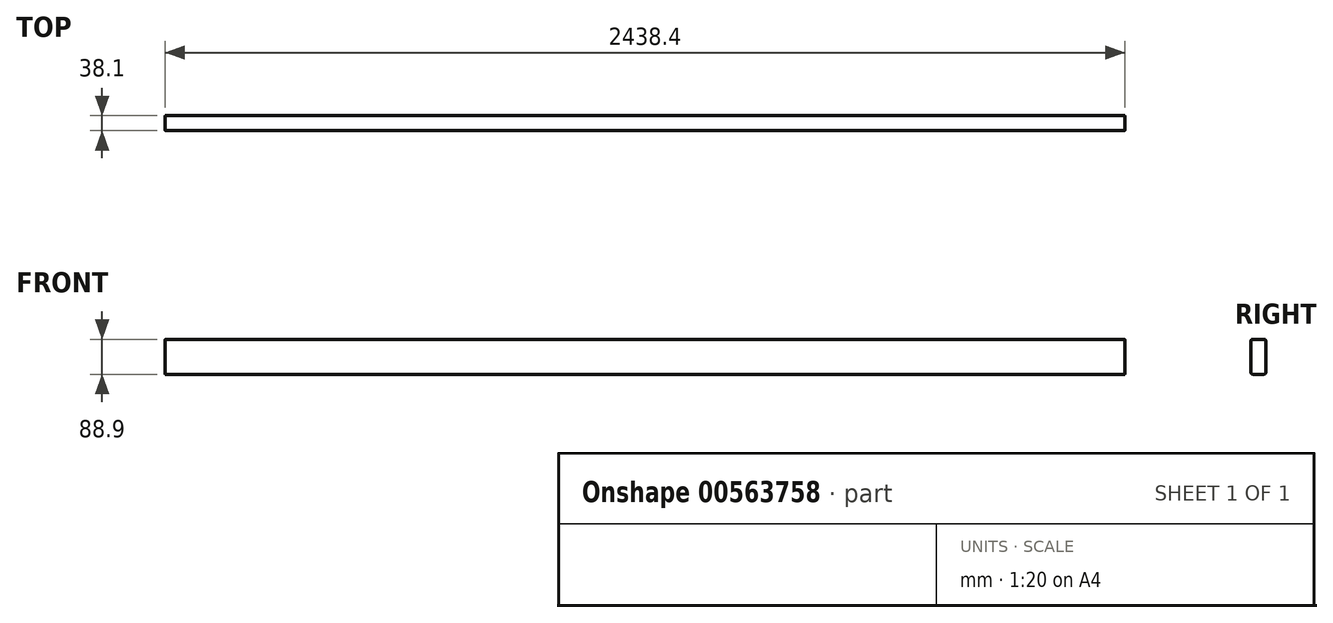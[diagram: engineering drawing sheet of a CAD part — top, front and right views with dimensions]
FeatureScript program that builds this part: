
annotation { "Feature Type Name" : "Feature", "Feature Type Description" : "" }
export const myFeature = defineFeature(function(context is Context, id is Id, definition is map)
    precondition{}
    {
        {
            var Q0;
            Q0=qCreatedBy(makeId("Right.planeOp"),FACE);
            var sketch = newSketch(context, id + "F0", { "sketchPlane" : qUnion([Q0])});
            skLineSegment(sketch, "E0.bottom", {"start": v(19.05, -44.45) * mm, "end": v(-19.05, -44.45) * mm});
            skLineSegment(sketch, "E0.top", {"start": v(19.05, 44.45) * mm, "end": v(-19.05, 44.45) * mm});
            skLineSegment(sketch, "E0.left", {"start": v(19.05, -44.45) * mm, "end": v(19.05, 44.45) * mm});
            skLineSegment(sketch, "E0.right", {"start": v(-19.05, -44.45) * mm, "end": v(-19.05, 44.45) * mm});
            skPoint(sketch, "E0.middle", {"position": v(0, 0) * mm});
            skSolve(sketch);
        }
        {
            var Q0;
            Q0=qSketchRegion(id+"F0",true);
            extrude(context, id + "F1", {"entities" : qUnion([Q0]), "endBound" : BoundingType.SYMMETRIC, "depth" : 2438.4 * mm, "offsetDistance" : 25.4 * mm});
        }
        {
            var Q0;
            Q0=makeQuery(id+"F1.opExtrude","SWEPT_EDGE",EDGE,{"disambiguationData":[OSD([sQuery(id+"F0.wireOp",EDGE,"E0.top"),sQuery(id+"F0.wireOp",EDGE,"E0.right")])]});
            var Q1;
            Q1=makeQuery(id+"F1.opExtrude","SWEPT_EDGE",EDGE,{"disambiguationData":[OSD([sQuery(id+"F0.wireOp",EDGE,"E0.top"),sQuery(id+"F0.wireOp",EDGE,"E0.left")])]});
            var Q2;
            Q2=makeQuery(id+"F1.opExtrude","SWEPT_EDGE",EDGE,{"disambiguationData":[OSD([sQuery(id+"F0.wireOp",EDGE,"E0.bottom"),sQuery(id+"F0.wireOp",EDGE,"E0.right")])]});
            var Q3;
            Q3=makeQuery(id+"F1.opExtrude","SWEPT_EDGE",EDGE,{"disambiguationData":[OSD([sQuery(id+"F0.wireOp",EDGE,"E0.bottom"),sQuery(id+"F0.wireOp",EDGE,"E0.left")])]});
            fillet(context, id + "F2", {"entities" : qUnion([Q0, Q1, Q2, Q3]), "radius" : 5.08 * mm, "tangentPropagation" : true, "allowEdgeOverflow" : false});
        }
    });
